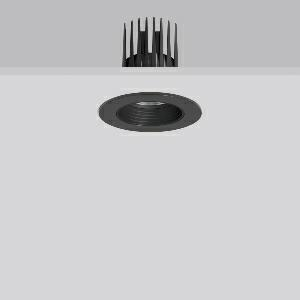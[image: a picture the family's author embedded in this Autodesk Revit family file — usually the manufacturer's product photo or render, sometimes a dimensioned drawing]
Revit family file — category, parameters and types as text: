
# Revit family: heledon_mini_e_901752_003_3754
name_source: partatom
category: Lighting Fixtures
units: mm (PartAtom-declared; Revit-internal decimal feet)

## family parameters
Cut with Voids When Loaded = No
Host = Face
Light Source = No
Part Type = Normal
Room Calculation Point = No
Round Connector Dimension = Use Diameter
Shared = No

## types (1)
- HELEDON mini E (1 x LED Modul 930, 3000 lm, 3000)
    Apparent Load = 29 VA
    Approval mark = CE
    CIE Flux Codes = 96 100 100 100 100
    Color Rendering = 90
    Color Temperature = 3000
    Default Elevation = 1800 mm
    Description = Series: HELEDON mini
Round recessed downlight. Housing: die-cast aluminium, powder-coated. Black plastic ring and recessed LED to prevent glare from the side. Optical assembly with lens made of plastic (polycarbonate) for the best homogeneous light distribution - can be changed without tools. Best colour rendering index Ra>90. Suitable for Recessed ceiling mounting. Installation without tools thanks to spring fastening system. Including separate LED converter with connecting cable 600 mm.High quality converter without flickering and stroboscopic effect. Through-wiring box (5 pole) available as accessory. The following accessories can be mounted without use of tools: interchangeable lenses, decorative glasses, honeycomb louvre, clear and frosted diffusers, white interchangeable plastic ring. 
Colour: deep black, matt (RAL 9005)
Diameter: 124 mm
Height: 3 mm
Cut-out diameter: 114 mm
Recess height: 170 mm
Luminaire: recess height: 120 mm
Lamp: LED
Socket: without socket
Colour temperature: 3000K
Colour rendering index (CRI): 92
System power: 29 W
Rated luminous flux: 3000 lm
Luminous efficiency: 103 lm/W
Control gear: Regulated power supply
Protection class: II
Type of protection: IP 20
    Height = 0 mm  [stored 0 ft]
    Lamp = 1 x LED Modul 930
    Lamp Light Flux = 3000 lm
    Lamp count = 1
    Length = 124 mm  [stored 0.406824 ft]
    Lifetime = 50000 h
    Luminous efficacy = 103 lm/W
    Manufacturer = RZB
    ModVariant = No
    Model = 901752.003
    Mounting Place = Ceiling
    Mounting Type = Recessed
    Number of Poles = 1
    OnlyDefault = Yes
    Power Factor = 1
    Product Name = HELEDON mini E
    Product group = Recessed downlights
    ProductGroupID = 402
    Protection Class = Protection class II
    Protection Degree = IP 20
    RLX_Detail_Level = 1
    RLX_Emergency_Light_Flux = 0 lm
    RLX_Emergency_Type = 0
    RLX_Emergency_Type_DB = No
    RlxData = <blob elided: 125769 chars, md5=80077da8>
    Socket = socket
    Standby Power = 0 W
    System Light Flux = 3000 lm
    System Power = 29 W
    Type Comments = Product without accessories
    Type Image = 901656.003.jpg
    URL = http://relux.com
    VarID = ---
    Voltage = 230 V
    Voltage Range = 220-240 V
    Weight = 0.00 kg
    Width = 0 mm  [stored 0 ft]

note: [stored X ft] marks values corroborated as IEEE doubles in the binary element streams (Revit-internal decimal feet)

## geometry (parser evidence)
native form markers: Blend x4, Sweep x11
no freeform markers — native parametric forms only
